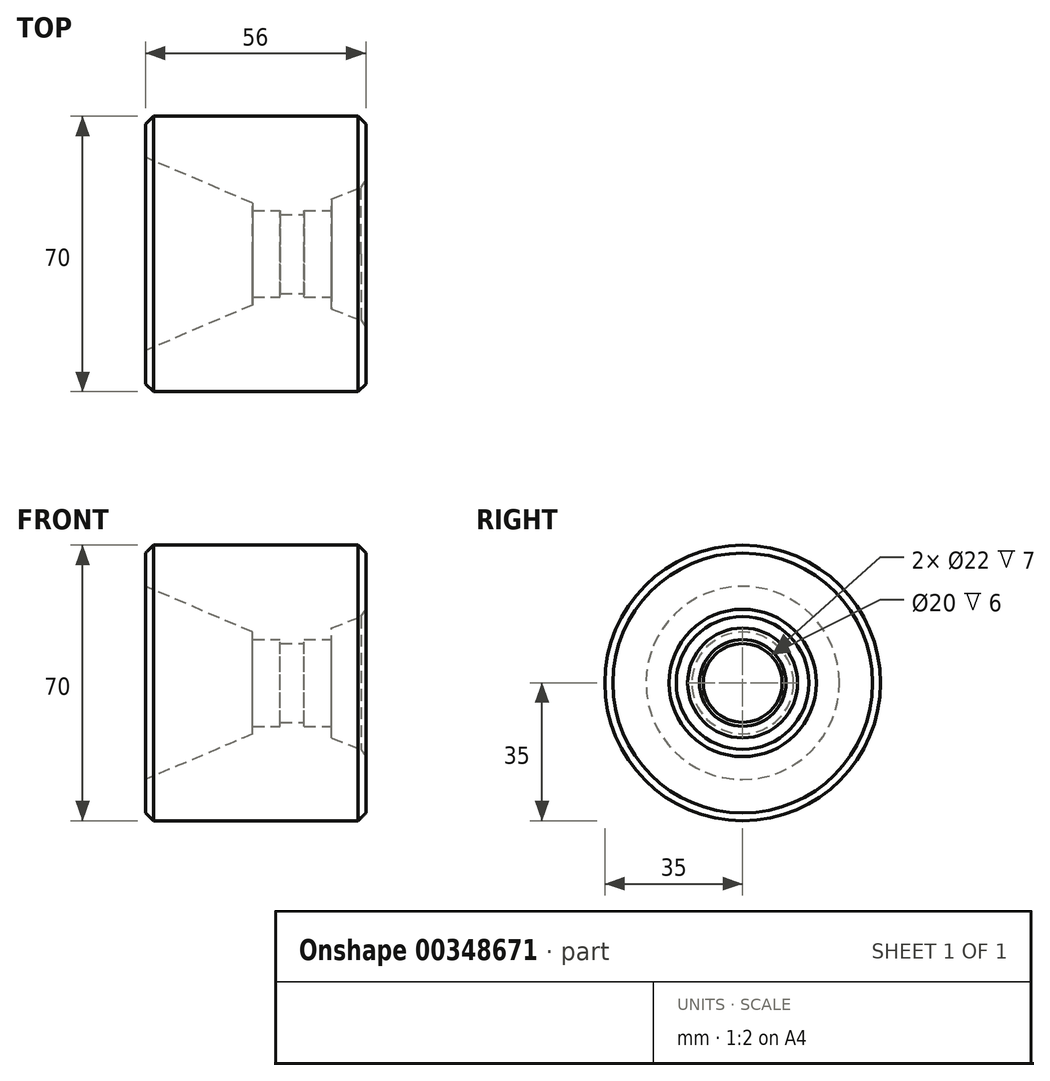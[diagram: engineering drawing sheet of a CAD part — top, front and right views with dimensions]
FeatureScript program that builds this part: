
annotation { "Feature Type Name" : "Feature", "Feature Type Description" : "" }
export const myFeature = defineFeature(function(context is Context, id is Id, definition is map)
    precondition{}
    {
        {
            var Q0;
            Q0=qCreatedBy(makeId("Front.planeOp"),FACE);
            var sketch = newSketch(context, id + "F0", { "sketchPlane" : qUnion([Q0])});
            skLineSegment(sketch, "E0", {"start": v(-8.77, 11) * mm, "end": v(-8.77, 13.96) * mm});
            skLineSegment(sketch, "E1", {"start": v(-8.77, 13.96) * mm, "end": v(0, 17.33) * mm});
            skLineSegment(sketch, "E2", {"start": v(0, 17.33) * mm, "end": v(0, 35) * mm});
            skLineSegment(sketch, "E3", {"start": v(0, 35) * mm, "end": v(-56, 35) * mm});
            skLineSegment(sketch, "E4", {"start": v(-56, 35) * mm, "end": v(-56, 24.55) * mm});
            skLineSegment(sketch, "E5", {"start": v(-56, 24.55) * mm, "end": v(-28.77, 12.93) * mm});
            skLineSegment(sketch, "E6", {"start": v(-28.77, 12.93) * mm, "end": v(-28.77, 11) * mm});
            skLineSegment(sketch, "E7", {"start": v(-21.77, 10) * mm, "end": v(-15.77, 10) * mm});
            skLineSegment(sketch, "E8", {"start": v(32.3, 0) * mm, "end": v(-70.75, 0) * mm, "construction": true});
            skLineSegment(sketch, "E9", {"start": v(-21.77, 10) * mm, "end": v(-21.77, 11) * mm});
            skLineSegment(sketch, "E10", {"start": v(-21.77, 11) * mm, "end": v(-28.77, 11) * mm});
            skLineSegment(sketch, "E11", {"start": v(-15.77, 10) * mm, "end": v(-15.77, 11) * mm});
            skLineSegment(sketch, "E12", {"start": v(-15.77, 11) * mm, "end": v(-8.77, 11) * mm});
            skSolve(sketch);
        }
        {
            var Q0;
            Q0 = qSketchRegion(id + "F0", true);
            var Q1;
            Q1=sQuery(id+"F0.wireOp",EDGE,"E8");
            revolve(context, id + "F1", {"entities" : qUnion([Q0]), "axis" : qUnion([Q1]), "revolveType" : RevolveType.FULL});
        }
        {
            var Q0;
            Q0=makeQuery(id+"F1.opRevolve","SWEPT_EDGE",EDGE,{"disambiguationData":[OSD([sQuery(id+"F0.wireOp",EDGE,"E2"),sQuery(id+"F0.wireOp",EDGE,"E3")])]});
            var Q1;
            Q1=makeQuery(id+"F1.opRevolve","SWEPT_EDGE",EDGE,{"disambiguationData":[OSD([sQuery(id+"F0.wireOp",EDGE,"E3"),sQuery(id+"F0.wireOp",EDGE,"E4")])]});
            var Q2;
            Q2=makeQuery(id+"F1.opRevolve","SWEPT_EDGE",EDGE,{"disambiguationData":[OSD([sQuery(id+"F0.wireOp",EDGE,"E1"),sQuery(id+"F0.wireOp",EDGE,"E2")])]});
            chamfer(context, id + "F2", {"entities" : qUnion([Q0, Q1, Q2]), "width" : 2 * mm, "tangentPropagation" : true});
        }
    });
